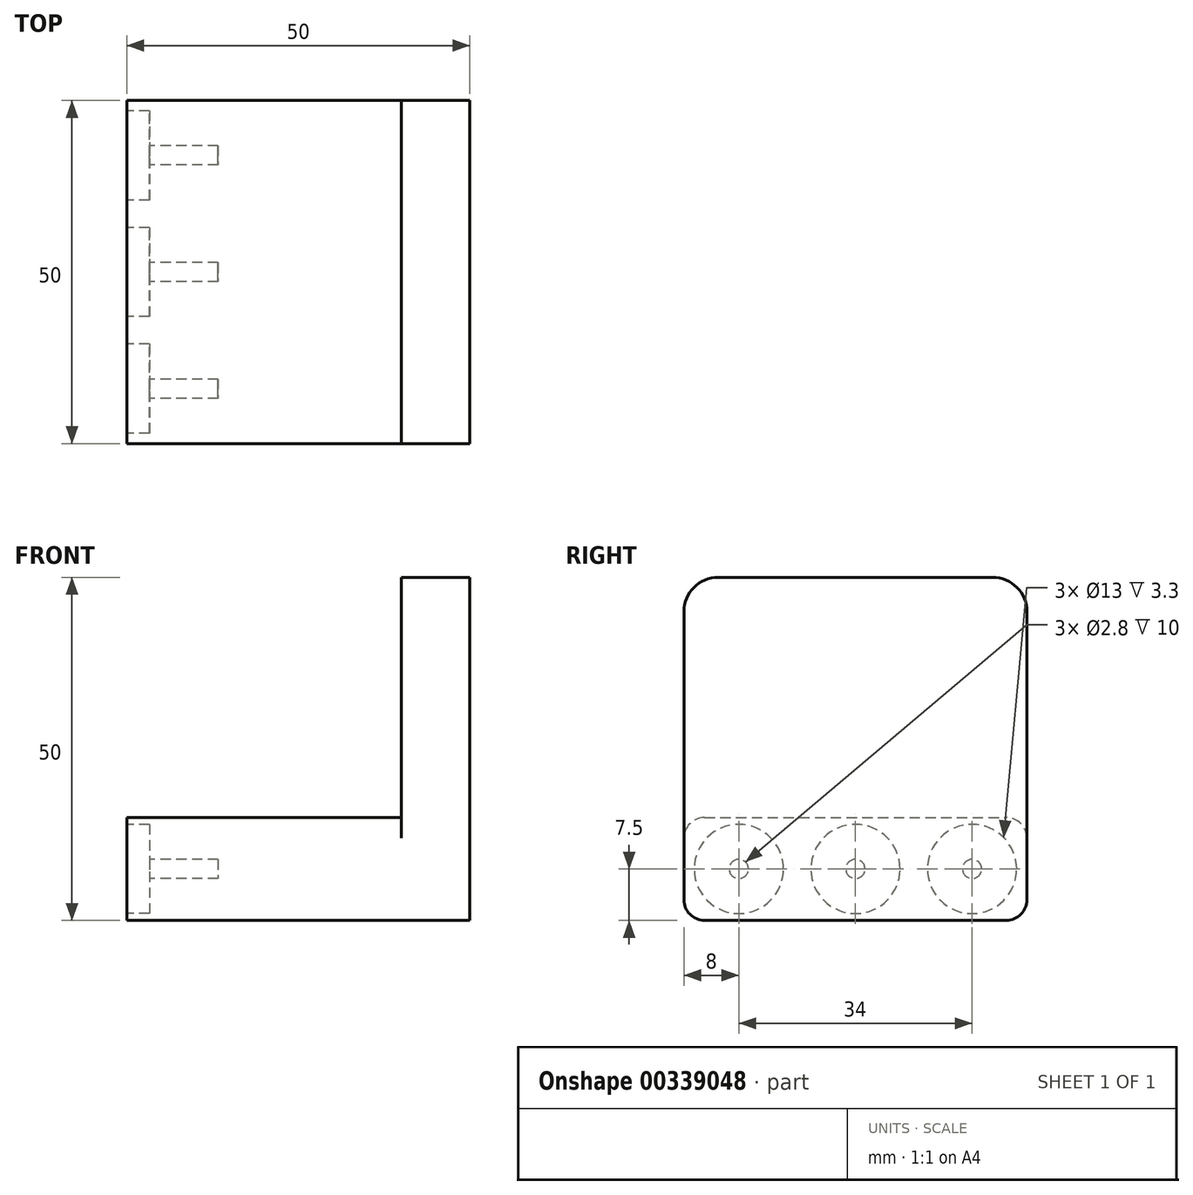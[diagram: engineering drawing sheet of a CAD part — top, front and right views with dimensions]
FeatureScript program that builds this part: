
annotation { "Feature Type Name" : "Feature", "Feature Type Description" : "" }
export const myFeature = defineFeature(function(context is Context, id is Id, definition is map)
    precondition{}
    {
        {
            var Q0;
            Q0=qCreatedBy(makeId("Front.planeOp"),FACE);
            var sketch = newSketch(context, id + "F0", { "sketchPlane" : qUnion([Q0])});
            skLineSegment(sketch, "E0", {"start": v(-50, 0) * mm, "end": v(0, 0) * mm});
            skLineSegment(sketch, "E1", {"start": v(0, 0) * mm, "end": v(0, 50) * mm});
            skLineSegment(sketch, "E2", {"start": v(0, 50) * mm, "end": v(-10, 50) * mm});
            skLineSegment(sketch, "E3", {"start": v(-10, 50) * mm, "end": v(-10, 15) * mm});
            skLineSegment(sketch, "E4", {"start": v(-10, 15) * mm, "end": v(-50, 15) * mm});
            skLineSegment(sketch, "E5", {"start": v(-50, 15) * mm, "end": v(-50, 0) * mm});
            skSolve(sketch);
        }
        {
            var Q0;
            Q0 = qSketchRegion(id + "F0", true);
            extrude(context, id + "F1", {"entities" : qUnion([Q0]), "depth" : 50 * mm});
        }
        {
            var Q0;
            Q0=makeQuery(id+"F1.opExtrude","CAP_EDGE",EDGE,{"disambiguationData":[OSD([sQuery(id+"F0.wireOp",EDGE,"E2")])],"isStart":false});
            var Q1;
            Q1=makeQuery(id+"F1.opExtrude","CAP_EDGE",EDGE,{"disambiguationData":[OSD([sQuery(id+"F0.wireOp",EDGE,"E2")])],"isStart":true});
            fillet(context, id + "F2", {"entities" : qUnion([Q0, Q1]), "radius" : 5 * mm, "tangentPropagation" : true, "allowEdgeOverflow" : false});
        }
        {
            var Q0;
            Q0=makeQuery(id+"F1.opExtrude","SWEPT_FACE",FACE,{"disambiguationData":[OSD([sQuery(id+"F0.wireOp",EDGE,"E5")])]});
            var sketch = newSketch(context, id + "F3", { "sketchPlane" : qUnion([Q0])});
            skCircle(sketch, "E6", {"center": v(8, 7.5) * mm, "radius": 6.5 * mm});
            skPoint(sketch, "E6.centerSnap0", {"position": v(0, 7.5) * mm});
            skCircle(sketch, "E7", {"center": v(25, 7.5) * mm, "radius": 6.5 * mm});
            skCircle(sketch, "E8", {"center": v(42, 7.5) * mm, "radius": 6.5 * mm});
            skLineSegment(sketch, "E9", {"start": v(8, 7.5) * mm, "end": v(25, 7.5) * mm, "construction": true});
            skLineSegment(sketch, "E10", {"start": v(25, 7.5) * mm, "end": v(42, 7.5) * mm, "construction": true});
            skLineSegment(sketch, "E11", {"start": v(25, 15) * mm, "end": v(25, 7.5) * mm, "construction": true});
            skCircle(sketch, "E12", {"center": v(8, 7.5) * mm, "radius": 1.4 * mm});
            skCircle(sketch, "E13", {"center": v(25, 7.5) * mm, "radius": 1.4 * mm});
            skCircle(sketch, "E14", {"center": v(42, 7.5) * mm, "radius": 1.4 * mm});
            skSolve(sketch);
        }
        {
            var Q0;
            Q0 = qSketchRegion(id + "F3", true);
            var Q1;
            Q1=makeQuery(id+"F3.imprint","IMPRINT",FACE,{"disambiguationData":[TD([[makeQuery(id+"F3.imprint","IMPRINT",EDGE,{"derivedFrom":sQuery(id+"F3.wireOp",EDGE,"E12")}),1.0]])]});
            var Q2;
            Q2=makeQuery(id+"F3.imprint","IMPRINT",FACE,{"disambiguationData":[TD([[makeQuery(id+"F3.imprint","IMPRINT",EDGE,{"derivedFrom":sQuery(id+"F3.wireOp",EDGE,"E13")}),1.0]])]});
            var Q3;
            Q3=makeQuery(id+"F3.imprint","IMPRINT",FACE,{"disambiguationData":[TD([[makeQuery(id+"F3.imprint","IMPRINT",EDGE,{"derivedFrom":sQuery(id+"F3.wireOp",EDGE,"E14")}),1.0]])]});
            extrude(context, id + "F4", {"entities" : qUnion([Q0, Q1, Q2, Q3]), "operationType" : NewBodyOperationType.REMOVE, "oppositeDirection" : true, "depth" : 3.3 * mm});
        }
        {
            var Q0;
            Q0=makeQuery(id+"F3.imprint","IMPRINT",FACE,{"disambiguationData":[TD([[makeQuery(id+"F3.imprint","IMPRINT",EDGE,{"derivedFrom":sQuery(id+"F3.wireOp",EDGE,"E12")}),1.0]])]});
            var Q1;
            Q1=makeQuery(id+"F3.imprint","IMPRINT",FACE,{"disambiguationData":[TD([[makeQuery(id+"F3.imprint","IMPRINT",EDGE,{"derivedFrom":sQuery(id+"F3.wireOp",EDGE,"E13")}),1.0]])]});
            var Q2;
            Q2=makeQuery(id+"F3.imprint","IMPRINT",FACE,{"disambiguationData":[TD([[makeQuery(id+"F3.imprint","IMPRINT",EDGE,{"derivedFrom":sQuery(id+"F3.wireOp",EDGE,"E14")}),1.0]])]});
            extrude(context, id + "F5", {"entities" : qUnion([Q0, Q1, Q2]), "operationType" : NewBodyOperationType.REMOVE, "oppositeDirection" : true, "depth" : (3.3 + 10) * mm});
        }
        {
            var Q0;
            Q0=makeQuery(id+"F1.opExtrude","CAP_EDGE",EDGE,{"disambiguationData":[OSD([sQuery(id+"F0.wireOp",EDGE,"E0")])],"isStart":false});
            var Q1;
            Q1=makeQuery(id+"F1.opExtrude","CAP_EDGE",EDGE,{"disambiguationData":[OSD([sQuery(id+"F0.wireOp",EDGE,"E0")])],"isStart":true});
            var Q2;
            Q2=makeQuery(id+"F1.opExtrude","CAP_EDGE",EDGE,{"disambiguationData":[OSD([sQuery(id+"F0.wireOp",EDGE,"E4")])],"isStart":true});
            var Q3;
            Q3=makeQuery(id+"F1.opExtrude","CAP_EDGE",EDGE,{"disambiguationData":[OSD([sQuery(id+"F0.wireOp",EDGE,"E4")])],"isStart":false});
            fillet(context, id + "F6", {"entities" : qUnion([Q0, Q1, Q2, Q3]), "radius" : 3 * mm, "tangentPropagation" : true, "allowEdgeOverflow" : false});
        }
    });
